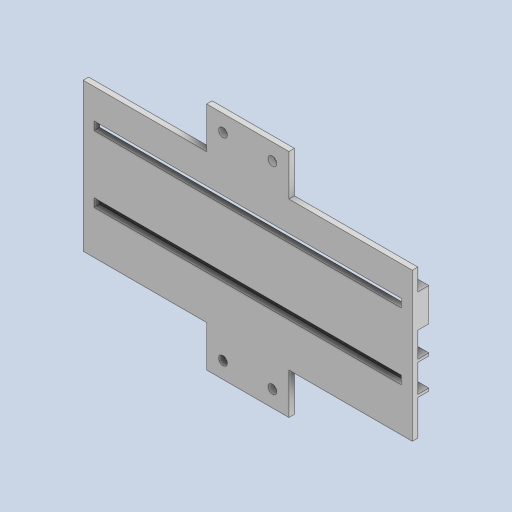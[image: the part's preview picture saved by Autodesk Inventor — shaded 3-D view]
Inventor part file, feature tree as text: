
AUTODESK INVENTOR PART (.ipt)
format: ipt  version: 2023 (Build 270158000, 158)  size: 209,920 bytes
history: native  units: in
note: dims shown in document units (in); Inventor stores cm internally (conversion verified against a paired STEP export)
features: extrude x2, other x1, sketch x1
ambient origin geometry x8: Origin, YZ Plane, XZ Plane, XY Plane, X Axis, Y Axis, Z Axis, Center Point
bodies: Body1 (feature_tree)
feature tree (4):
  other  "ソリッド1"
  extrude  "押し出し1"  Depth=1.1811in
  extrude  "押し出し4"  Depth=0.2953in
  sketch  "スケッチ3"
